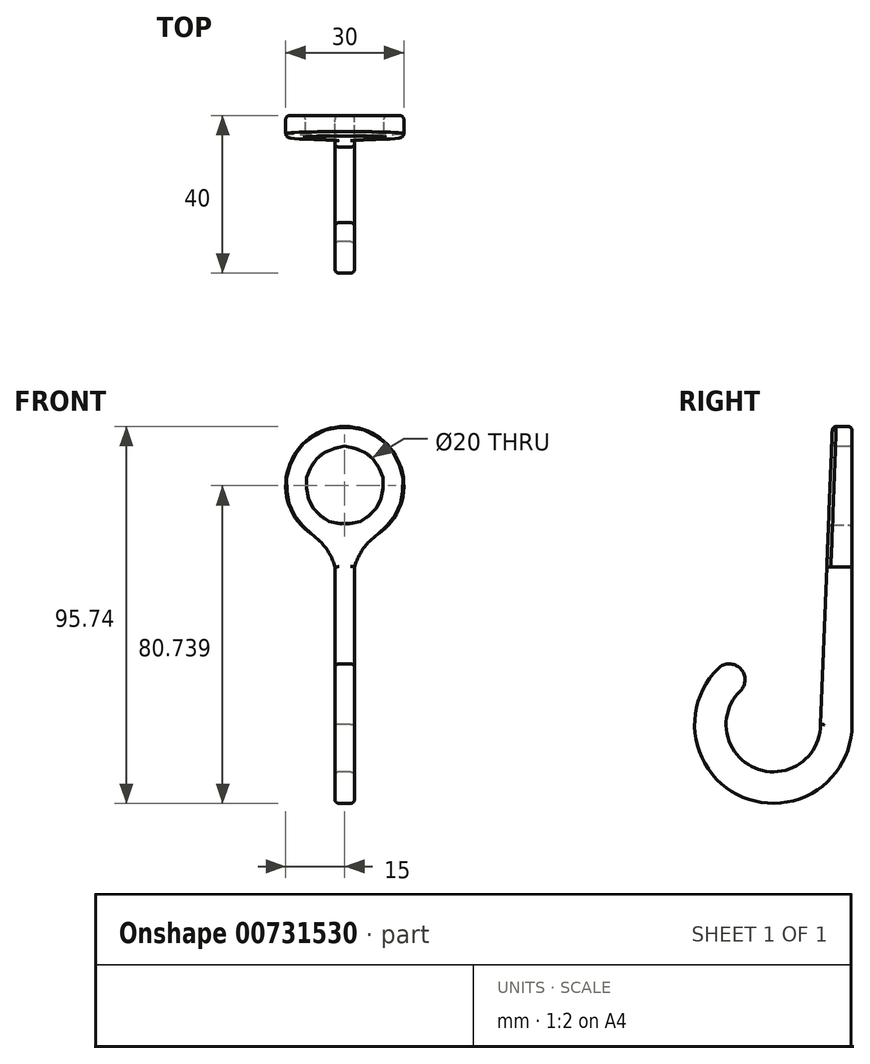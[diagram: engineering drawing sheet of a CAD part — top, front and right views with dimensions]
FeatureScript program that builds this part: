
annotation { "Feature Type Name" : "Feature", "Feature Type Description" : "" }
export const myFeature = defineFeature(function(context is Context, id is Id, definition is map)
    precondition{}
    {
        {
            var Q0;
            Q0=qCreatedBy(makeId("Front.planeOp"),FACE);
            var sketch = newSketch(context, id + "F0", { "sketchPlane" : qUnion([Q0])});
            skLineSegment(sketch, "E0.right", {"start": v(2.49, 11.36) * mm, "end": v(2.49, -30.83) * mm});
            skLineSegment(sketch, "E1.top", {"start": v(2.49, -30.83) * mm, "end": v(-2.5, -30.83) * mm});
            skLineSegment(sketch, "E1.right", {"start": v(-2.5, 11.36) * mm, "end": v(-2.5, -30.83) * mm});
            skArc(sketch, "E2", {"start": v(8.36, 17.46) * mm, "mid": v(4.67, 13.85) * mm, "end": v(2.49, 9.17) * mm});
            skArc(sketch, "E3.MirrorCS", {"start": v(-8.37, 17.46) * mm, "mid": v(-4.68, 13.86) * mm, "end": v(-2.5, 9.18) * mm});
            skLineSegment(sketch, "E4", {"start": v(-2.5, 9.18) * mm, "end": v(2.49, 9.17) * mm});
            skCircle(sketch, "E5", {"center": v(0, 29.9) * mm, "radius": 10 * mm});
            skCircle(sketch, "E6", {"center": v(0, 29.9) * mm, "radius": 15 * mm});
            skLineSegment(sketch, "E7", {"start": v(-2.5, 11.36) * mm, "end": v(2.49, 11.36) * mm});
            skSolve(sketch);
        }
        {
            var Q0;
            Q0=makeQuery(id+"F0.imprint","IMPRINT",FACE,{"disambiguationData":[TD([[makeQuery(id+"F0.imprint","IMPRINT",EDGE,{"derivedFrom":sQuery(id+"F0.wireOp",EDGE,"E5")}),-1.0]])]});
            var Q1;
            {var subQ0=sQuery(id+"F0.wireOp",EDGE,"E2");Q1=makeQuery(id+"F0.imprint","IMPRINT",FACE,{"disambiguationData":[TD([[makeQuery(id+"F0.imprint","IMPRINT",EDGE,{"derivedFrom":subQ0}),-1.0]])]});}
            extrude(context, id + "F1", {"entities" : qUnion([Q0, Q1]), "depth" : 5 * mm, "offsetDistance" : 25 * mm});
        }
        {
            var Q0;
            Q0=qCreatedBy(makeId("Right.planeOp"),FACE);
            var sketch = newSketch(context, id + "F2", { "sketchPlane" : qUnion([Q0])});
            skLineSegment(sketch, "E8.0", {"start": v(0, 11.36) * mm, "end": v(0, -30.83) * mm});
            skLineSegment(sketch, "E9", {"start": v(0, 44.9) * mm, "end": v(-5, 44.9) * mm});
            skLineSegment(sketch, "E10.0", {"start": v(0, 11.36) * mm, "end": v(0, 44.9) * mm});
            skPoint(sketch, "E11.orphan", {"position": v(0, 14.9) * mm});
            skPoint(sketch, "E12.start.orphan", {"position": v(0, 39.9) * mm});
            skArc(sketch, "E13", {"start": v(-34, -16.55) * mm, "mid": v(-27.74, -49.27) * mm, "end": v(0, -30.83) * mm});
            skArc(sketch, "E14.0", {"start": v(-28.4, -22.26) * mm, "mid": v(-24.65, -41.9) * mm, "end": v(-8, -30.83) * mm});
            skArc(sketch, "E15", {"start": v(-28.4, -22.26) * mm, "mid": v(-28.35, -16.6) * mm, "end": v(-34, -16.55) * mm});
            skLineSegment(sketch, "E16", {"start": v(-8, -30.83) * mm, "end": v(-5, 44.9) * mm});
            skLineSegment(sketch, "E17", {"start": v(0, 11.36) * mm, "end": v(-6.33, 11.36) * mm});
            skSolve(sketch);
        }
        {
            var Q0;
            Q0=makeQuery(id+"F2.imprint","IMPRINT",FACE,{"disambiguationData":[TD([[makeQuery(id+"F2.imprint","IMPRINT",EDGE,{"derivedFrom":sQuery(id+"F2.wireOp",EDGE,"w04mwDkx-DsZz-m4Nu-nIuf-thKjT2vUk3fw")}),1.0]])]});
            var Q1;
            Q1=makeQuery(id+"F2.imprint","IMPRINT",FACE,{"disambiguationData":[TD([[makeQuery(id+"F2.imprint","IMPRINT",EDGE,{"derivedFrom":sQuery(id+"F2.wireOp",EDGE,"E8.0")}),-1.0]])]});
            var Q2;
            {var subQ0=sQuery(id+"F2.wireOp",EDGE,"QX2yePzY-QqVM-gUIs-EyW7-y1pm9Z3eRD08");Q2=makeQuery(id+"F2.imprint","IMPRINT",FACE,{"disambiguationData":[TD([[makeQuery(id+"F2.imprint","IMPRINT",EDGE,{"derivedFrom":subQ0}),-1.0]])]});}
            extrude(context, id + "F3", {"entities" : qUnion([Q0, Q1, Q2]), "operationType" : NewBodyOperationType.ADD, "endBound" : BoundingType.SYMMETRIC, "depth" : 5 * mm, "offsetDistance" : 25 * mm});
        }
        {
            var Q0;
            Q0=makeQuery(id+"F1.opExtrude","CAP_FACE",FACE,{"disambiguationData":[OSD([sQuery(id+"F0.wireOp",EDGE,"E2"),sQuery(id+"F0.wireOp",EDGE,"E3.MirrorCS"),sQuery(id+"F0.wireOp",EDGE,"E4"),sQuery(id+"F0.wireOp",EDGE,"E5"),sQuery(id+"F0.wireOp",EDGE,"E6")])],"isStart":false});
            var Q1;
            Q1=makeQuery(id+"F3.opExtrude","SWEPT_FACE",FACE,{"disambiguationData":[OSD([sQuery(id+"F2.wireOp",EDGE,"E16")])]});
            extrude(context, id + "F4", {"entities" : qUnion([Q0]), "operationType" : NewBodyOperationType.ADD, "endBound" : BoundingType.UP_TO_SURFACE, "depth" : 25 * mm, "endBoundEntityFace" : qUnion([Q1]), "offsetDistance" : 25 * mm});
        }
        {
            var Q0;
            {var subQ0=sQuery(id+"F0.wireOp",EDGE,"E5");Q0=makeQuery(id+"F4.boolean.opBoolean","MERGE",FACE,{"derivedFrom":[makeQuery(id+"F1.opExtrude","SWEPT_FACE",FACE,{"disambiguationData":[OSD([subQ0])]}),makeQuery(id+"F4.opExtrude","SWEPT_FACE",FACE,{"disambiguationData":[OSD([subQ0])]})]});}
            var Q1;
            Q1=makeQuery(id+"F1.opExtrude","CAP_EDGE",EDGE,{"disambiguationData":[OSD([sQuery(id+"F0.wireOp",EDGE,"E6")])],"isStart":true});
            var Q2;
            {var subQ0=sQuery(id+"F0.wireOp",EDGE,"E6");Q2=makeQuery(id+"F4.boolean.opBoolean","MERGE",EDGE,{"derivedFrom":[makeQuery(id+"F4.opExtrude","CAP_EDGE",EDGE,{"disambiguationData":[OSD([subQ0]),OD(0.0)],"isStart":false}),makeQuery(id+"F4.opExtrude","CAP_EDGE",EDGE,{"disambiguationData":[OSD([subQ0]),OD(1.0)],"isStart":false})]});}
            fillet(context, id + "F5", {"entities" : qUnion([Q0, Q1, Q2]), "radius" : 1 * mm, "tangentPropagation" : true, "allowEdgeOverflow" : false});
        }
        {
            var Q0;
            Q0=makeQuery(id+"F3.opExtrude","CAP_EDGE",EDGE,{"disambiguationData":[OSD([sQuery(id+"F2.wireOp",EDGE,"E13")])],"isStart":false});
            var Q1;
            Q1=makeQuery(id+"F3.opExtrude","CAP_EDGE",EDGE,{"disambiguationData":[OSD([sQuery(id+"F2.wireOp",EDGE,"E13")])],"isStart":true});
            var Q2;
            Q2=makeQuery(id+"F3.opExtrude","CAP_EDGE",EDGE,{"disambiguationData":[OSD([sQuery(id+"F2.wireOp",EDGE,"E16")])],"isStart":true});
            var Q3;
            Q3=makeQuery(id+"F3.opExtrude","CAP_EDGE",EDGE,{"disambiguationData":[OSD([sQuery(id+"F2.wireOp",EDGE,"E16")])],"isStart":false});
            fillet(context, id + "F6", {"entities" : qUnion([Q0, Q1, Q2, Q3]), "radius" : 1 * mm, "tangentPropagation" : true, "allowEdgeOverflow" : false});
        }
    });
